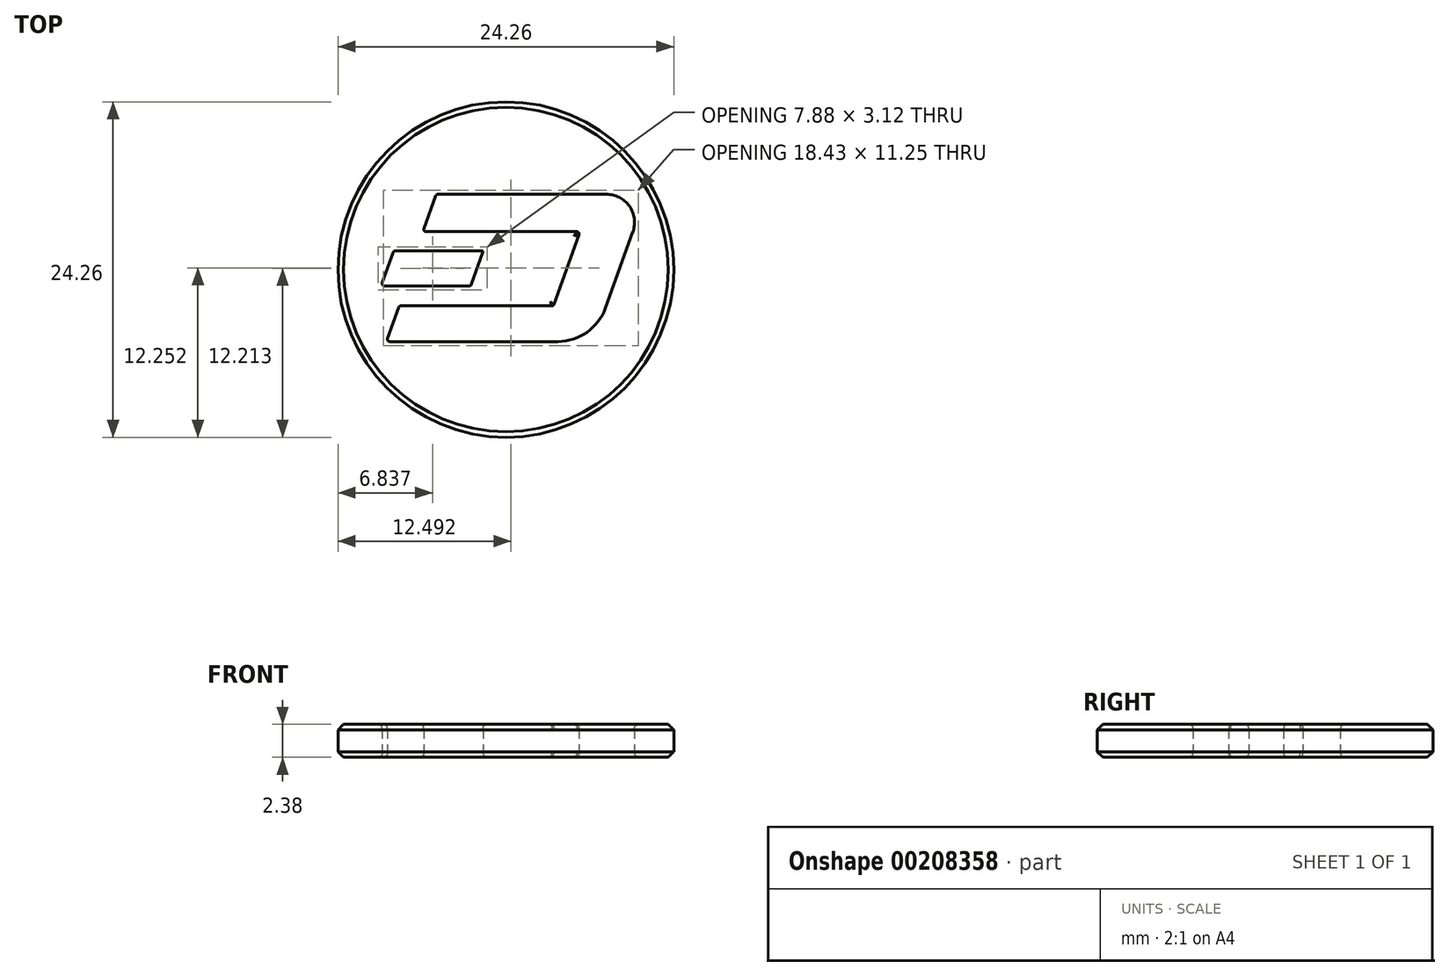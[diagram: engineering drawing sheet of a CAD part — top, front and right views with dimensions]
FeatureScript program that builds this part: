
annotation { "Feature Type Name" : "Feature", "Feature Type Description" : "" }
export const myFeature = defineFeature(function(context is Context, id is Id, definition is map)
    precondition{}
    {
        {
            var Q0;
            Q0=qCreatedBy(makeId("Top.planeOp"),FACE);
            var sketch = newSketch(context, id + "F0", { "sketchPlane" : qUnion([Q0])});
            skCircle(sketch, "E0", {"center": v(0, 0) * mm, "radius": 12.12 * mm});
            skLineSegment(sketch, "E1", {"start": v(-4.9, 5.45) * mm, "end": v(7.26, 5.45) * mm});
            skLineSegment(sketch, "E2", {"start": v(9.17, 2.73) * mm, "end": v(7.2, -2.78) * mm});
            skLineSegment(sketch, "E3", {"start": v(3.75, -5.2) * mm, "end": v(-8.4, -5.2) * mm});
            skLineSegment(sketch, "E4", {"start": v(-8.55, -5) * mm, "end": v(-7.73, -2.72) * mm});
            skLineSegment(sketch, "E5", {"start": v(-7.59, -2.62) * mm, "end": v(3.32, -2.62) * mm});
            skLineSegment(sketch, "E6", {"start": v(3.46, -2.52) * mm, "end": v(5.28, 2.53) * mm});
            skLineSegment(sketch, "E7", {"start": v(5.13, 2.74) * mm, "end": v(-5.77, 2.74) * mm});
            skLineSegment(sketch, "E8", {"start": v(-5.91, 2.94) * mm, "end": v(-5.05, 5.35) * mm});
            skLineSegment(sketch, "E9", {"start": v(-8, 1.34) * mm, "end": v(-1.7, 1.34) * mm});
            skLineSegment(sketch, "E10", {"start": v(-1.66, 1.27) * mm, "end": v(-2.48, -1.07) * mm});
            skLineSegment(sketch, "E11", {"start": v(-2.63, -1.18) * mm, "end": v(-8.78, -1.18) * mm});
            skLineSegment(sketch, "E12", {"start": v(-8.92, -0.97) * mm, "end": v(-8.15, 1.24) * mm});
            skPoint(sketch, "E13.visualSharp", {"position": v(10.43, 5.45) * mm});
            skArc(sketch, "E13.filletArc", {"start": v(9.17, 2.73) * mm, "mid": v(8.92, 4.59) * mm, "end": v(7.26, 5.45) * mm});
            skPoint(sketch, "E14.visualSharp", {"position": v(6.6, -5.2) * mm});
            skArc(sketch, "E14.filletArc", {"start": v(3.75, -5.2) * mm, "mid": v(5.85, -4.54) * mm, "end": v(7.2, -2.78) * mm});
            skPoint(sketch, "E15.visualSharp", {"position": v(-5.02, 5.45) * mm});
            skArc(sketch, "E15.filletArc", {"start": v(-4.9, 5.45) * mm, "mid": v(-5, 5.42) * mm, "end": v(-5.05, 5.35) * mm});
            skPoint(sketch, "E16.visualSharp", {"position": v(-5.99, 2.74) * mm});
            skArc(sketch, "E16.filletArc", {"start": v(-5.91, 2.94) * mm, "mid": v(-5.9, 2.8) * mm, "end": v(-5.77, 2.74) * mm});
            skPoint(sketch, "E17.visualSharp", {"position": v(-8.11, 1.34) * mm});
            skArc(sketch, "E17.filletArc", {"start": v(-8, 1.34) * mm, "mid": v(-8.1, 1.31) * mm, "end": v(-8.15, 1.24) * mm});
            skPoint(sketch, "E18.visualSharp", {"position": v(-1.63, 1.34) * mm});
            skArc(sketch, "E18.filletArc", {"start": v(-1.66, 1.27) * mm, "mid": v(-1.66, 1.32) * mm, "end": v(-1.7, 1.34) * mm});
            skPoint(sketch, "E19.visualSharp", {"position": v(-2.52, -1.18) * mm});
            skArc(sketch, "E19.filletArc", {"start": v(-2.63, -1.18) * mm, "mid": v(-2.54, -1.15) * mm, "end": v(-2.48, -1.07) * mm});
            skPoint(sketch, "E20.visualSharp", {"position": v(-9, -1.18) * mm});
            skArc(sketch, "E20.filletArc", {"start": v(-8.92, -0.97) * mm, "mid": v(-8.9, -1.11) * mm, "end": v(-8.78, -1.18) * mm});
            skPoint(sketch, "E21.visualSharp", {"position": v(5.35, 2.74) * mm});
            skArc(sketch, "E21.filletArc", {"start": v(5.28, 2.53) * mm, "mid": v(5.26, 2.67) * mm, "end": v(5.13, 2.74) * mm});
            skPoint(sketch, "E22.visualSharp", {"position": v(3.43, -2.62) * mm});
            skArc(sketch, "E22.filletArc", {"start": v(3.32, -2.62) * mm, "mid": v(3.4, -2.6) * mm, "end": v(3.46, -2.52) * mm});
            skPoint(sketch, "E23.visualSharp", {"position": v(-7.7, -2.62) * mm});
            skArc(sketch, "E23.filletArc", {"start": v(-7.59, -2.62) * mm, "mid": v(-7.68, -2.65) * mm, "end": v(-7.73, -2.72) * mm});
            skPoint(sketch, "E24.visualSharp", {"position": v(-8.62, -5.2) * mm});
            skArc(sketch, "E24.filletArc", {"start": v(-8.55, -5) * mm, "mid": v(-8.53, -5.14) * mm, "end": v(-8.4, -5.2) * mm});
            skSolve(sketch);
        }
        {
            var Q0;
            Q0=makeQuery(id+"F0.imprint","IMPRINT",FACE,{"disambiguationData":[TD([[makeQuery(id+"F0.imprint","IMPRINT",EDGE,{"derivedFrom":sQuery(id+"F0.wireOp",EDGE,"E0")}),1.0]])]});
            extrude(context, id + "F1", {"entities" : qUnion([Q0]), "endBound" : BoundingType.SYMMETRIC, "depth" : 2.38 * mm});
        }
        {
            var Q0;
            Q0=makeQuery(id+"F1.opExtrude","CAP_EDGE",EDGE,{"disambiguationData":[OSD([sQuery(id+"F0.wireOp",EDGE,"E0")])],"isStart":false});
            var Q1;
            Q1=makeQuery(id+"F1.opExtrude","CAP_EDGE",EDGE,{"disambiguationData":[OSD([sQuery(id+"F0.wireOp",EDGE,"E0")])],"isStart":true});
            chamfer(context, id + "F2", {"entities" : qUnion([Q0, Q1]), "width" : .4 * mm, "tangentPropagation" : true});
        }
        {
            var Q0;
            Q0=makeQuery(id+"F1.opExtrude","CAP_EDGE",EDGE,{"disambiguationData":[OSD([sQuery(id+"F0.wireOp",EDGE,"E1")])],"isStart":false});
            var Q1;
            Q1=makeQuery(id+"F1.opExtrude","CAP_EDGE",EDGE,{"disambiguationData":[OSD([sQuery(id+"F0.wireOp",EDGE,"E9")])],"isStart":false});
            var Q2;
            Q2=makeQuery(id+"F1.opExtrude","CAP_EDGE",EDGE,{"disambiguationData":[OSD([sQuery(id+"F0.wireOp",EDGE,"E5")])],"isStart":true});
            var Q3;
            Q3=makeQuery(id+"F1.opExtrude","CAP_EDGE",EDGE,{"disambiguationData":[OSD([sQuery(id+"F0.wireOp",EDGE,"E11")])],"isStart":true});
            fillet(context, id + "F3", {"entities" : qUnion([Q0, Q1, Q2, Q3]), "radius" : .3 * mm, "tangentPropagation" : true, "allowEdgeOverflow" : false});
        }
    });
